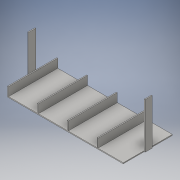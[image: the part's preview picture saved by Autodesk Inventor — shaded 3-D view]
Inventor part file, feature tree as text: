
AUTODESK INVENTOR PART (.ipt)
format: ipt  version: 2016 (Build 200138000, 138)  size: 157,184 bytes
history: native  units: in
note: dims shown in document units (in); Inventor stores cm internally (conversion verified against a paired STEP export)
features: extrude x7, sketch x7
ambient origin geometry x8: Origin, YZ Plane, XZ Plane, XY Plane, X Axis, Y Axis, Z Axis, Center Point
bodies: Solid1 (feature_tree)
feature tree (14):
  extrude  "Extrusion1"  Depth=0.063in
  extrude  "Extrusion2"  Depth=0.063in
  extrude  "Extrusion3"  Depth=0.063in
  extrude  "Extrusion4"  Depth=0.063in
  extrude  "Extrusion5"  Depth=0.063in
  extrude  "Extrusion6"  Depth=0.5in
  extrude  "Extrusion7"  Depth=0.063in TaperAngle=0.0deg
  sketch  "Sketch1"  dims[d0=8.0in d1=0.063in]
  sketch  "Sketch2"  dims[d2=3.4in d3=0.0in d4=0.063in]
  sketch  "Sketch3"  dims[d5=0.6in d6=0.0in d7=0.063in]
  sketch  "Sketch4"  dims[d8=0.6in d9=0.0in d10=0.063in]
  sketch  "Sketch5"  dims[d11=0.6in d12=0.0in d13=0.063in]
  sketch  "Sketch6"  dims[d14=0.6in d15=0.0in d16=0.5in]
  sketch  "Sketch7"  dims[d17=3.15in d18=0.063in d19=0.0in d20=3.15in d21=0.063in d22=0.0in]
